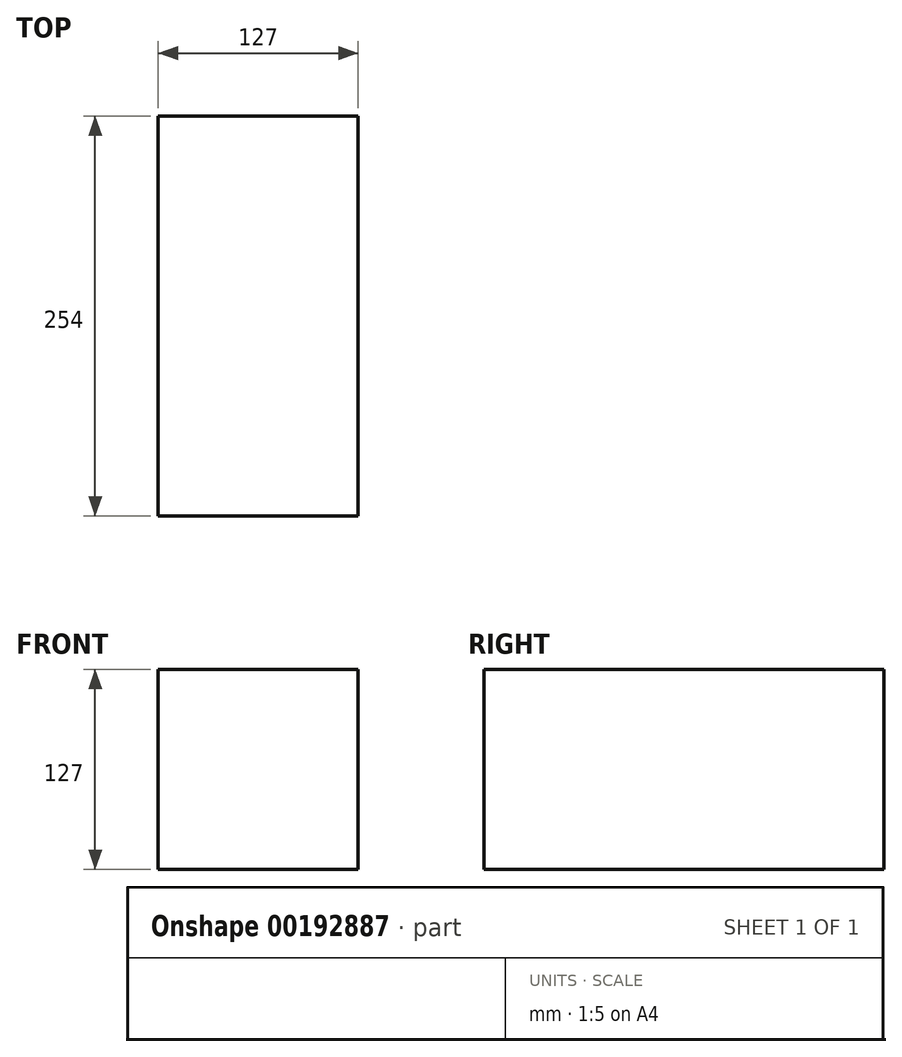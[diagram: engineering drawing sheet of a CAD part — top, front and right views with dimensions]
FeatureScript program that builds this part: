
annotation { "Feature Type Name" : "Feature", "Feature Type Description" : "" }
export const myFeature = defineFeature(function(context is Context, id is Id, definition is map)
    precondition{}
    {
        {
            var Q0;
            Q0=qCreatedBy(makeId("Front.planeOp"),FACE);
            var sketch = newSketch(context, id + "F0", { "sketchPlane" : qUnion([Q0])});
            skLineSegment(sketch, "E0.bottom", {"start": v(-69.54, -63.5) * mm, "end": v(57.46, -63.5) * mm});
            skLineSegment(sketch, "E0.top", {"start": v(-69.54, 63.5) * mm, "end": v(57.46, 63.5) * mm});
            skLineSegment(sketch, "E0.left", {"start": v(-69.54, -63.5) * mm, "end": v(-69.54, 63.5) * mm});
            skLineSegment(sketch, "E0.right", {"start": v(57.46, -63.5) * mm, "end": v(57.46, 63.5) * mm});
            skPoint(sketch, "E0.middle", {"position": v(-6.04, 0) * mm});
            skSolve(sketch);
        }
        {
            var Q0;
            Q0=makeQuery(id+"F0.imprint","IMPRINT",FACE,{"disambiguationData":[TD([[makeQuery(id+"F0.imprint","IMPRINT",EDGE,{"derivedFrom":sQuery(id+"F0.wireOp",EDGE,"E0.bottom")}),1.0]])]});
            extrude(context, id + "F1", {"entities" : qUnion([Q0]), "depth" : 127 * mm});
        }
        {
            var Q0;
            Q0=makeQuery(id+"F1.opExtrude","CAP_FACE",FACE,{"disambiguationData":[OSD([sQuery(id+"F0.wireOp",EDGE,"E0.bottom"),sQuery(id+"F0.wireOp",EDGE,"E0.top"),sQuery(id+"F0.wireOp",EDGE,"E0.left"),sQuery(id+"F0.wireOp",EDGE,"E0.right")])],"isStart":false});
            extrude(context, id + "F2", {"entities" : qUnion([Q0]), "operationType" : NewBodyOperationType.ADD, "depth" : 127 * mm});
        }
    });
